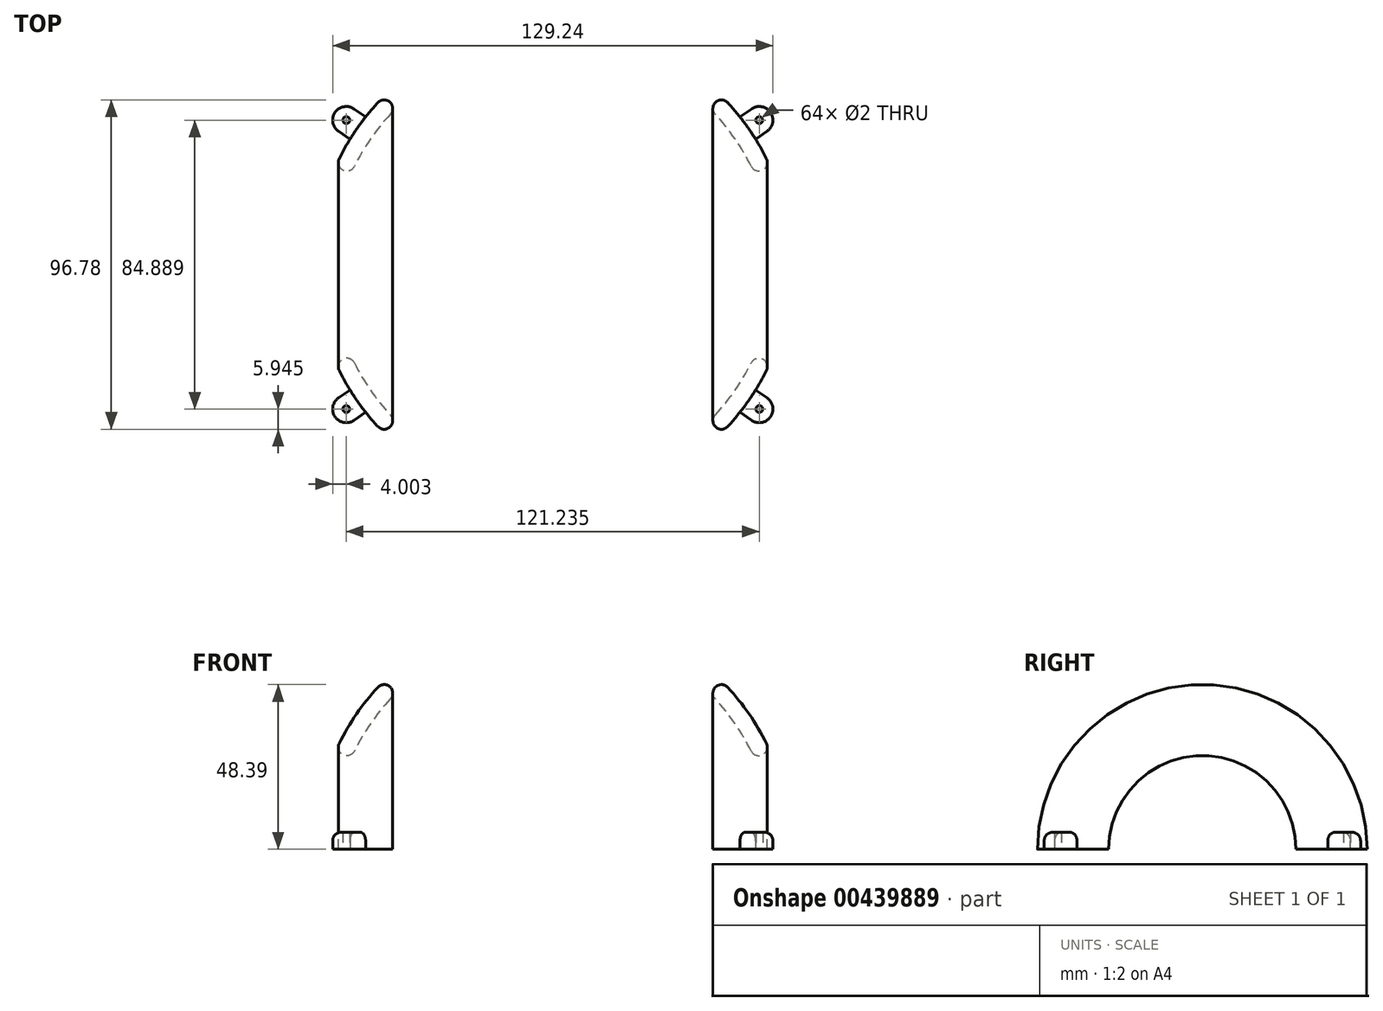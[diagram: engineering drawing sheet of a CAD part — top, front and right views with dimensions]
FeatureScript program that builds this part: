
annotation { "Feature Type Name" : "Feature", "Feature Type Description" : "" }
export const myFeature = defineFeature(function(context is Context, id is Id, definition is map)
    precondition{}
    {
        {
            var Q0;
            Q0=qCreatedBy(makeId("Top.planeOp"),FACE);
            var sketch = newSketch(context, id + "F0", { "sketchPlane" : qUnion([Q0])});
            skArc(sketch, "E0", {"start": v(70, 0) * mm, "mid": v(0, 70) * mm, "end": v(-70, 0) * mm});
            skLineSegment(sketch, "E1", {"start": v(-70, 0) * mm, "end": v(70, 0) * mm});
            skSolve(sketch);
        }
        {
            var Q0;
            Q0=makeQuery(id+"F0.imprint","IMPRINT",FACE,{"disambiguationData":[TD([[makeQuery(id+"F0.imprint","IMPRINT",EDGE,{"derivedFrom":sQuery(id+"F0.wireOp",EDGE,"E0")}),1.0]])]});
            var Q1;
            Q1=sQuery(id+"F0.wireOp",EDGE,"E1");
            revolve(context, id + "F1", {"entities" : qUnion([Q0]), "axis" : qUnion([Q1]), "revolveType" : RevolveType.ONE_DIRECTION, "angle" : 180 * degree});
        }
        {
            var Q0;
            Q0=makeQuery(id+"F1.opRevolve","CAP_FACE",FACE,{"disambiguationData":[OSD([sQuery(id+"F0.wireOp",EDGE,"E0"),sQuery(id+"F0.wireOp",EDGE,"E1")])],"isStart":true});
            shell(context, id + "F2", {"entities" : qUnion([Q0]), "thickness" : 5 * mm});
        }
        {
            var Q0;
            Q0=qCreatedBy(makeId("Right.planeOp"),FACE);
            var sketch = newSketch(context, id + "F3", { "sketchPlane" : qUnion([Q0])});
            skCircle(sketch, "E2", {"center": v(0, 0) * mm, "radius": 27.5 * mm});
            skSolve(sketch);
        }
        {
            var Q0;
            Q0=qSketchRegion(id+"F3",true);
            extrude(context, id + "F4", {"entities" : qUnion([Q0]), "operationType" : NewBodyOperationType.REMOVE, "endBound" : BoundingType.SYMMETRIC, "depth" : 188 * mm});
        }
        {
            var Q0;
            Q0=makeQuery(id+"F4.boolean.opBoolean","INTERSECT",EDGE,{"disambiguationData":[OD(1.0)],"derivedFrom":[makeQuery(id+"F1.opRevolve","SWEPT_FACE",FACE,{"disambiguationData":[OSD([sQuery(id+"F0.wireOp",EDGE,"E0")])]}),makeQuery(id+"F4.opExtrude","SWEPT_FACE",FACE,{"disambiguationData":[OSD([sQuery(id+"F3.wireOp",EDGE,"E2")])]})]});
            var Q1;
            Q1=makeQuery(id+"F4.boolean.opBoolean","INTERSECT",EDGE,{"disambiguationData":[OD(0.0)],"derivedFrom":[makeQuery(id+"F2.opShell","OFFSET_FACE",FACE,{"disambiguationData":[OSD([sQuery(id+"F0.wireOp",EDGE,"E0")])]}),makeQuery(id+"F4.opExtrude","SWEPT_FACE",FACE,{"disambiguationData":[OSD([sQuery(id+"F3.wireOp",EDGE,"E2")])]})]});
            var Q2;
            Q2=makeQuery(id+"F4.boolean.opBoolean","INTERSECT",EDGE,{"disambiguationData":[OD(0.0)],"derivedFrom":[makeQuery(id+"F1.opRevolve","SWEPT_FACE",FACE,{"disambiguationData":[OSD([sQuery(id+"F0.wireOp",EDGE,"E0")])]}),makeQuery(id+"F4.opExtrude","SWEPT_FACE",FACE,{"disambiguationData":[OSD([sQuery(id+"F3.wireOp",EDGE,"E2")])]})]});
            var Q3;
            Q3=makeQuery(id+"F4.boolean.opBoolean","INTERSECT",EDGE,{"disambiguationData":[OD(1.0)],"derivedFrom":[makeQuery(id+"F2.opShell","OFFSET_FACE",FACE,{"disambiguationData":[OSD([sQuery(id+"F0.wireOp",EDGE,"E0")])]}),makeQuery(id+"F4.opExtrude","SWEPT_FACE",FACE,{"disambiguationData":[OSD([sQuery(id+"F3.wireOp",EDGE,"E2")])]})]});
            fillet(context, id + "F5", {"entities" : qUnion([Q0, Q1, Q2, Q3]), "radius" : 2.5 * mm, "tangentPropagation" : true, "allowEdgeOverflow" : false});
        }
        {
            var Q0;
            Q0=qCreatedBy(makeId("Front.planeOp"),FACE);
            var sketch = newSketch(context, id + "F6", { "sketchPlane" : qUnion([Q0])});
            skLineSegment(sketch, "E3.bottom", {"start": v(47, 0) * mm, "end": v(-47, 0) * mm});
            skLineSegment(sketch, "E3.top", {"start": v(47, 150.47) * mm, "end": v(-47, 150.47) * mm});
            skLineSegment(sketch, "E3.left", {"start": v(47, 0) * mm, "end": v(47, 150.47) * mm});
            skLineSegment(sketch, "E3.right", {"start": v(-47, 0) * mm, "end": v(-47, 150.47) * mm});
            skSolve(sketch);
        }
        {
            var Q0;
            Q0=qSketchRegion(id+"F6",true);
            extrude(context, id + "F7", {"entities" : qUnion([Q0]), "operationType" : NewBodyOperationType.REMOVE, "endBound" : BoundingType.SYMMETRIC, "oppositeDirection" : true, "depth" : 178 * mm});
        }
        {
            var Q0;
            Q0=makeQuery(id+"F7.boolean.opBoolean","INTERSECT",EDGE,{"derivedFrom":[makeQuery(id+"F1.opRevolve","SWEPT_FACE",FACE,{"disambiguationData":[OSD([sQuery(id+"F0.wireOp",EDGE,"E0")])]}),makeQuery(id+"F7.opExtrude","SWEPT_FACE",FACE,{"disambiguationData":[OSD([sQuery(id+"F6.wireOp",EDGE,"E3.left")])]})]});
            var Q1;
            Q1=makeQuery(id+"F7.boolean.opBoolean","INTERSECT",EDGE,{"derivedFrom":[makeQuery(id+"F2.opShell","OFFSET_FACE",FACE,{"disambiguationData":[OSD([sQuery(id+"F0.wireOp",EDGE,"E0")])]}),makeQuery(id+"F7.opExtrude","SWEPT_FACE",FACE,{"disambiguationData":[OSD([sQuery(id+"F6.wireOp",EDGE,"E3.left")])]})]});
            var Q2;
            Q2=makeQuery(id+"F7.boolean.opBoolean","INTERSECT",EDGE,{"derivedFrom":[makeQuery(id+"F2.opShell","OFFSET_FACE",FACE,{"disambiguationData":[OSD([sQuery(id+"F0.wireOp",EDGE,"E0")])]}),makeQuery(id+"F7.opExtrude","SWEPT_FACE",FACE,{"disambiguationData":[OSD([sQuery(id+"F6.wireOp",EDGE,"E3.right")])]})]});
            var Q3;
            Q3=makeQuery(id+"F7.boolean.opBoolean","INTERSECT",EDGE,{"derivedFrom":[makeQuery(id+"F1.opRevolve","SWEPT_FACE",FACE,{"disambiguationData":[OSD([sQuery(id+"F0.wireOp",EDGE,"E0")])]}),makeQuery(id+"F7.opExtrude","SWEPT_FACE",FACE,{"disambiguationData":[OSD([sQuery(id+"F6.wireOp",EDGE,"E3.right")])]})]});
            fillet(context, id + "F8", {"entities" : qUnion([Q0, Q1, Q2, Q3]), "radius" : 2.5 * mm, "tangentPropagation" : true, "allowEdgeOverflow" : false});
        }
        {
            var Q0;
            Q0=qCreatedBy(makeId("Top.planeOp"),FACE);
            var sketch = newSketch(context, id + "F9", { "sketchPlane" : qUnion([Q0])});
            skCircle(sketch, "E4", {"center": v(0, 0) * mm, "radius": 70 * mm});
            skLineSegment(sketch, "E5", {"start": v(87.04, -60.95) * mm, "end": v(0, 0) * mm, "construction": true});
            skLineSegment(sketch, "E6", {"start": v(-85.62, -59.95) * mm, "end": v(0, 0) * mm, "construction": true});
            skLineSegment(sketch, "E7", {"start": v(-78.61, 55.05) * mm, "end": v(0, 0) * mm, "construction": true});
            skLineSegment(sketch, "E8", {"start": v(86.06, 60.26) * mm, "end": v(0, 0) * mm, "construction": true});
            skArc(sketch, "E9", {"start": v(-58.32, 45.72) * mm, "mid": v(-63.9, 44.74) * mm, "end": v(-62.91, 39.17) * mm});
            skCircle(sketch, "E10", {"center": v(-60.62, 42.44) * mm, "radius": 1 * mm});
            skLineSegment(sketch, "E11", {"start": v(-58.32, 45.72) * mm, "end": v(-54.95, 43.36) * mm});
            skLineSegment(sketch, "E12.MirrorCS", {"start": v(-62.91, 39.17) * mm, "end": v(-59.54, 36.8) * mm});
            skLineSegment(sketch, "E13", {"start": v(0, 0) * mm, "end": v(0, 58.6) * mm, "construction": true});
            skCircle(sketch, "E14.MirrorC", {"center": v(60.62, 42.44) * mm, "radius": 1 * mm});
            skLineSegment(sketch, "E15.MirrorCS", {"start": v(58.32, 45.72) * mm, "end": v(54.95, 43.36) * mm});
            skLineSegment(sketch, "E16.MirrorCS", {"start": v(62.91, 39.17) * mm, "end": v(59.54, 36.8) * mm});
            skArc(sketch, "E17.MirrorCS", {"start": v(58.32, 45.72) * mm, "mid": v(63.9, 44.74) * mm, "end": v(62.91, 39.17) * mm});
            skCircle(sketch, "E18.MirrorC", {"center": v(60.62, -42.44) * mm, "radius": 1 * mm});
            skLineSegment(sketch, "E19.MirrorCS", {"start": v(58.32, -45.72) * mm, "end": v(54.95, -43.36) * mm});
            skLineSegment(sketch, "E20.MirrorCS", {"start": v(62.91, -39.17) * mm, "end": v(59.54, -36.8) * mm});
            skArc(sketch, "E21.MirrorCS", {"start": v(58.32, -45.72) * mm, "mid": v(63.9, -44.74) * mm, "end": v(62.91, -39.17) * mm});
            skCircle(sketch, "E22.MirrorC", {"center": v(-60.62, -42.44) * mm, "radius": 1 * mm});
            skLineSegment(sketch, "E23.MirrorCS", {"start": v(-62.91, -39.17) * mm, "end": v(-59.54, -36.8) * mm});
            skLineSegment(sketch, "E24.MirrorCS", {"start": v(-58.32, -45.72) * mm, "end": v(-54.95, -43.36) * mm});
            skArc(sketch, "E25.MirrorCS", {"start": v(-58.32, -45.72) * mm, "mid": v(-63.9, -44.74) * mm, "end": v(-62.91, -39.17) * mm});
            skSolve(sketch);
        }
        {
            var Q0;
            Q0=makeQuery(id+"F9.imprint","IMPRINT",FACE,{"disambiguationData":[TD([[makeQuery(id+"F9.imprint","IMPRINT",EDGE,{"derivedFrom":sQuery(id+"F9.wireOp",EDGE,"E9")}),1.0]])]});
            var Q1;
            {var subQ0=sQuery(id+"F9.wireOp",EDGE,"E15.MirrorCS");Q1=makeQuery(id+"F9.imprint","IMPRINT",FACE,{"disambiguationData":[TD([[makeQuery(id+"F9.imprint","IMPRINT",EDGE,{"derivedFrom":subQ0}),1.0]])]});}
            var Q2;
            {var subQ0=sQuery(id+"F9.wireOp",EDGE,"E19.MirrorCS");Q2=makeQuery(id+"F9.imprint","IMPRINT",FACE,{"disambiguationData":[TD([[makeQuery(id+"F9.imprint","IMPRINT",EDGE,{"derivedFrom":subQ0}),-1.0]])]});}
            var Q3;
            {var subQ0=sQuery(id+"F9.wireOp",EDGE,"E23.MirrorCS");Q3=makeQuery(id+"F9.imprint","IMPRINT",FACE,{"disambiguationData":[TD([[makeQuery(id+"F9.imprint","IMPRINT",EDGE,{"derivedFrom":subQ0}),-1.0]])]});}
            extrude(context, id + "F10", {"entities" : qUnion([Q0, Q1, Q2, Q3]), "depth" : 5 * mm});
        }
        {
            var Q0;
            Q0=makeQuery(id+"F10.opExtrude","CAP_EDGE",EDGE,{"disambiguationData":[OSD([sQuery(id+"F9.wireOp",EDGE,"E9")])],"isStart":false});
            var Q1;
            Q1=makeQuery(id+"F10.opExtrude","CAP_EDGE",EDGE,{"disambiguationData":[OSD([sQuery(id+"F9.wireOp",EDGE,"E25.MirrorCS")])],"isStart":false});
            var Q2;
            Q2=makeQuery(id+"F10.opExtrude","CAP_EDGE",EDGE,{"disambiguationData":[OSD([sQuery(id+"F9.wireOp",EDGE,"E21.MirrorCS")])],"isStart":false});
            var Q3;
            Q3=makeQuery(id+"F10.opExtrude","CAP_EDGE",EDGE,{"disambiguationData":[OSD([sQuery(id+"F9.wireOp",EDGE,"E17.MirrorCS")])],"isStart":false});
            fillet(context, id + "F11", {"entities" : qUnion([Q0, Q1, Q2, Q3]), "radius" : 2.5 * mm, "tangentPropagation" : true, "allowEdgeOverflow" : false});
        }
    });
